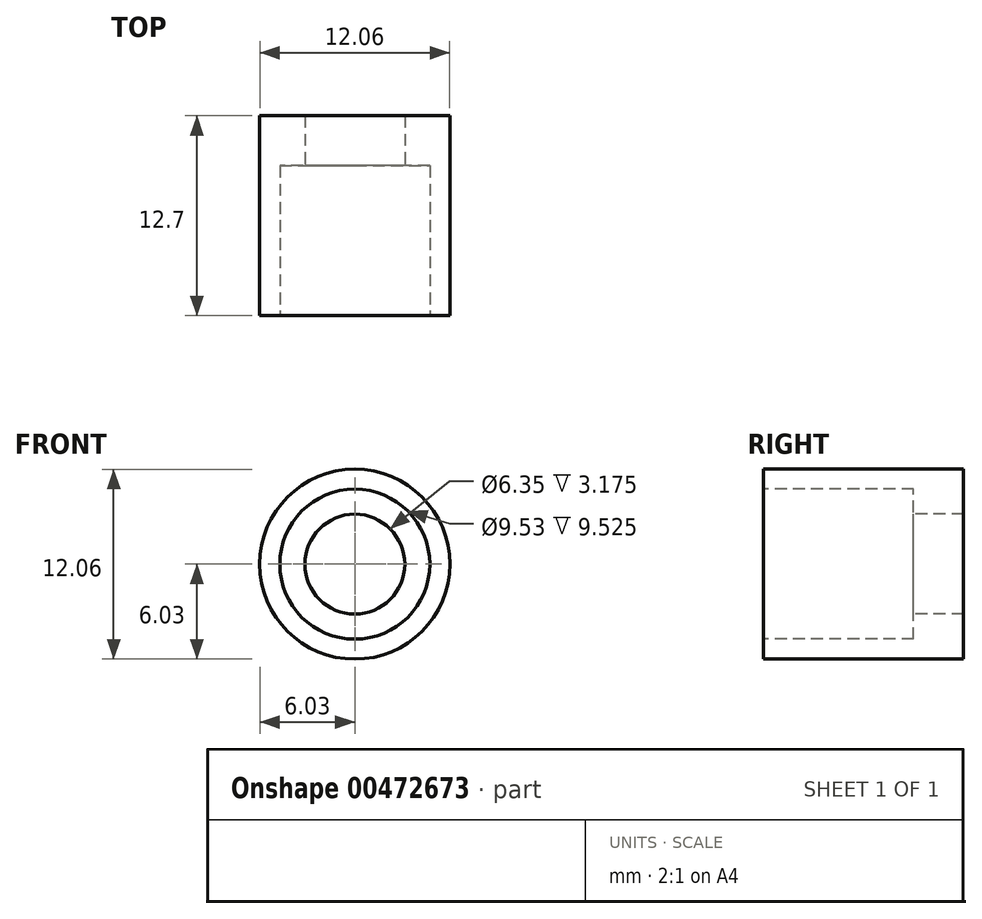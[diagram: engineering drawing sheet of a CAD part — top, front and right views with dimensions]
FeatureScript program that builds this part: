
annotation { "Feature Type Name" : "Feature", "Feature Type Description" : "" }
export const myFeature = defineFeature(function(context is Context, id is Id, definition is map)
    precondition{}
    {
        {
            var Q0;
            Q0=qCreatedBy(makeId("Top.planeOp"),FACE);
            var sketch = newSketch(context, id + "F0", { "sketchPlane" : qUnion([Q0])});
            skLineSegment(sketch, "E0", {"start": v(0, 0) * mm, "end": v(0, 12.7) * mm, "construction": true});
            skLineSegment(sketch, "E1", {"start": v(6.03, 12.7) * mm, "end": v(6.03, 0) * mm});
            skLineSegment(sketch, "E2", {"start": v(6.03, 0) * mm, "end": v(4.76, 0) * mm});
            skLineSegment(sketch, "E3", {"start": v(4.76, 0) * mm, "end": v(4.76, 9.53) * mm});
            skLineSegment(sketch, "E4", {"start": v(4.76, 9.53) * mm, "end": v(3.18, 9.53) * mm});
            skLineSegment(sketch, "E5", {"start": v(3.18, 9.53) * mm, "end": v(3.18, 12.7) * mm});
            skLineSegment(sketch, "E6", {"start": v(3.18, 12.7) * mm, "end": v(6.03, 12.7) * mm});
            skSolve(sketch);
        }
        {
            var Q0;
            Q0 = qSketchRegion(id + "F0", true);
            var Q1;
            Q1=sQuery(id+"F0.wireOp",EDGE,"E0");
            revolve(context, id + "F1", {"surfaceOperationType" : NewSurfaceOperationType.NEW, "entities" : qUnion([Q0]), "axis" : qUnion([Q1]), "revolveType" : RevolveType.FULL});
        }
    });
